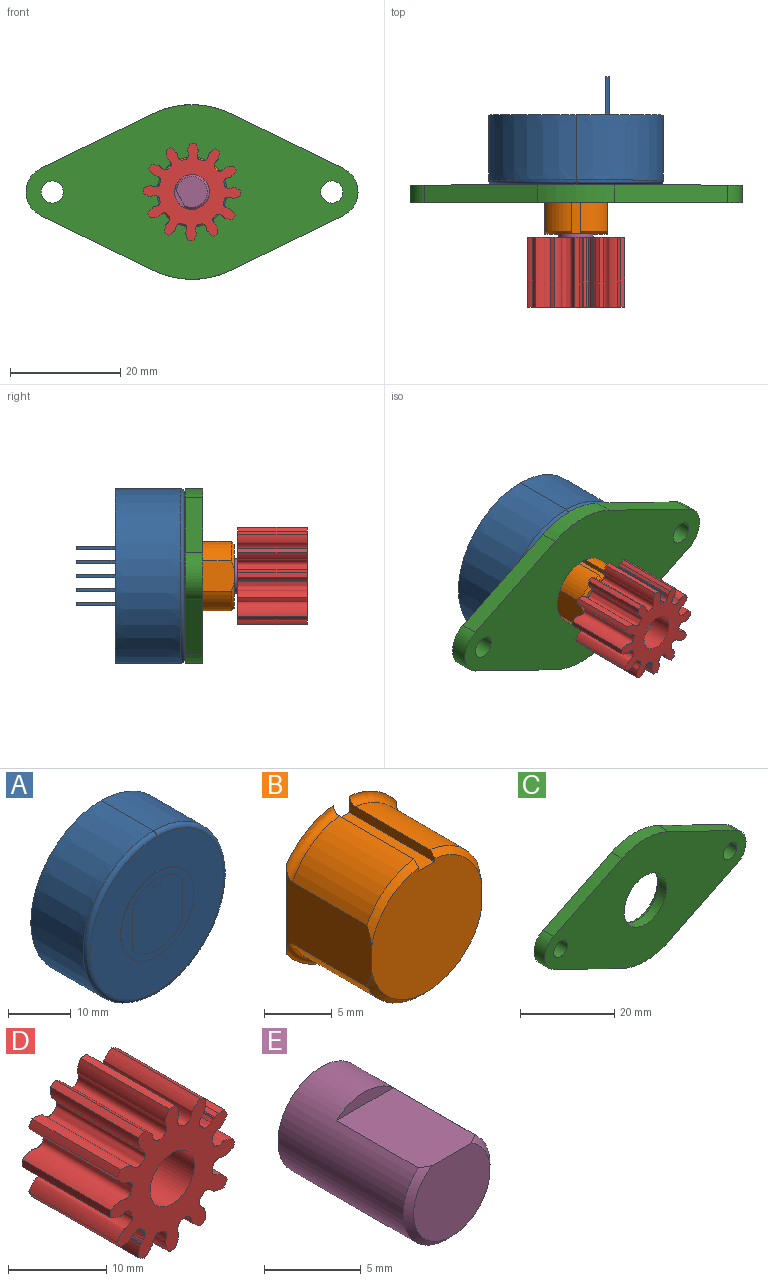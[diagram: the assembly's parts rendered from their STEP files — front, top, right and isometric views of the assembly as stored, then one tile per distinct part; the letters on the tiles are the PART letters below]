
ASSEMBLY  parts=5 mates=4
PART A: 35 faces, bbox 31.8x19.7x31.8 mm
  f0: plane 30.16x30.16mm, normal (0,-1,0), area 500mm2, adj f29,f30,f32,f33
  f1: plane 31.75x31.75mm, normal (0,1,0), area 789.7mm2, adj f2,f3,f5,f6,f7,f8,f10,f11
  f2: extruded ~31.75x15.88mm, area 589.6mm2, adj f1,f3,f32
  f3: extruded ~31.75x15.88mm, area 589.6mm2, adj f1,f2,f33
  f4: plane 0.64x0.64mm, normal (0,1,0), area 0.4mm2, adj f5,f6,f7,f8
  f5: plane 6.99x0.64mm, normal (0,0,-1), area 4.4mm2, adj f1,f4,f6,f8
  f6: plane 6.99x0.64mm, normal (1,0,0), area 4.4mm2, adj f1,f4,f5,f7
  f7: plane 6.99x0.64mm, normal (0,0,1), area 4.4mm2, adj f1,f4,f6,f8
  f8: plane 6.99x0.64mm, normal (-1,0,0), area 4.4mm2, adj f1,f4,f5,f7
  f9: plane 0.64x0.64mm, normal (0,1,0), area 0.4mm2, adj f10,f11,f12,f13
  f10: plane 6.99x0.64mm, normal (0,0,-1), area 4.4mm2, adj f1,f9,f11,f12
  f11: plane 6.99x0.64mm, normal (1,0,0), area 4.4mm2, adj f1,f9,f10,f13
  f12: plane 6.99x0.64mm, normal (-1,0,0), area 4.4mm2, adj f1,f9,f10,f13
  f13: plane 6.99x0.64mm, normal (0,0,1), area 4.4mm2, adj f1,f9,f11,f12
  f14: plane 0.64x0.64mm, normal (0,1,0), area 0.4mm2, adj f15,f16,f17,f18
  f15: plane 6.99x0.64mm, normal (-1,0,0), area 4.4mm2, adj f1,f14,f16,f17
  f16: plane 6.99x0.64mm, normal (0,0,1), area 4.4mm2, adj f1,f14,f15,f18
  f17: plane 6.99x0.64mm, normal (0,0,-1), area 4.4mm2, adj f1,f14,f15,f18
  f18: plane 6.99x0.64mm, normal (1,0,0), area 4.4mm2, adj f1,f14,f16,f17
  f19: plane 0.64x0.64mm, normal (0,1,0), area 0.4mm2, adj f20,f21,f22,f23
  f20: plane 6.99x0.64mm, normal (0,0,-1), area 4.4mm2, adj f1,f19,f21,f23
  f21: plane 6.99x0.64mm, normal (1,0,0), area 4.4mm2, adj f1,f19,f20,f22
  f22: plane 6.99x0.64mm, normal (0,0,1), area 4.4mm2, adj f1,f19,f21,f23
  f23: plane 6.99x0.64mm, normal (-1,0,0), area 4.4mm2, adj f1,f19,f20,f22
  f24: plane 0.64x0.64mm, normal (0,1,0), area 0.4mm2, adj f25,f26,f27,f28
  f25: plane 6.99x0.64mm, normal (0,0,-1), area 4.4mm2, adj f1,f24,f26,f28
  f26: plane 6.99x0.64mm, normal (1,0,0), area 4.4mm2, adj f1,f24,f25,f27
  f27: plane 6.99x0.64mm, normal (0,0,1), area 4.4mm2, adj f1,f24,f26,f28
  f28: plane 6.99x0.64mm, normal (-1,0,0), area 4.4mm2, adj f1,f24,f25,f27
  f29: extruded ~16.51x8.26mm, area 2.6mm2, adj f0,f30,f31
  f30: extruded ~16.51x8.26mm, area 2.6mm2, adj f0,f29,f31
  f31: plane 16.51x16.51mm, normal (0,-1,0), area 77.2mm2, adj f29,f30,f34
  f32: bspline ~31.75x25.88mm, area 61.3mm2, adj f0,f2,f33
  f33: bspline ~31.75x25.88mm, area 61.3mm2, adj f0,f3,f32
  f34: plane 13.92x11.43mm, normal (0,-1,0), area 136.9mm2, adj f31
PART B: 16 faces, bbox 14.5x8.9x16.1 mm
  f0: cone r=5.84mm half-angle=45deg, axis (0,1,0), area 10.7mm2, adj f3,f5,f13,f14
  f1: cone r=5.84mm half-angle=45deg, axis (0,1,0), area 4.7mm2, adj f3,f6,f12,f13
  f2: cone r=5.84mm half-angle=45deg, axis (0,1,0), area 4.7mm2, adj f3,f4,f10,f14
  f3: plane 11.62x11.43mm, normal (0,-1,0), area 106.2mm2, adj f0,f1,f2,f10,f11,f12,f13,f14
  f4: cylinder r=6.35mm len=7.75mm, axis (0,1,0), area 48.6mm2, adj f2,f9,f10,f14
  f5: cylinder r=6.35mm len=11.43mm, axis (0,1,0), area 110.2mm2, adj f0,f7,f13,f14
  f6: cylinder r=6.35mm len=7.75mm, axis (0,1,0), area 48.6mm2, adj f1,f8,f12,f13
  f7: torus R=6.99mm, axis (0,1,0), area 13.8mm2, adj f5,f13,f14,f15
  f8: torus R=6.99mm, axis (0,1,0), area 6.1mm2, adj f6,f12,f13,f15
  f9: torus R=6.99mm, axis (0,1,0), area 6.1mm2, adj f4,f10,f14,f15
  f10: plane 8.92x1.5mm, normal (-1,0,0), area 7.4mm2, adj f2,f3,f4,f9,f11,f15
  f11: plane 8.89x1.68mm, normal (0,0,1), area 14.9mm2, adj f3,f10,f12,f15
  f12: plane 8.92x1.5mm, normal (1,0,0), area 7.4mm2, adj f1,f3,f6,f8,f11,f15
  f13: plane 8.89x8.03mm, normal (-1,0,0), area 48.9mm2, adj f0,f1,f3,f5,f6,f7,f8,f15
  f14: plane 8.89x8.03mm, normal (1,0,0), area 48.9mm2, adj f0,f2,f3,f4,f5,f7,f9,f15
  f15: plane 13.92x11.43mm, normal (0,1,0), area 136.9mm2, adj f7,f8,f9,f10,f11,f12,f13,f14
PART C: 14 faces, bbox 60.3x3.2x31.8 mm
  f0: plane 20.54x9.99mm, normal (-0.44,0,-0.9), area 72.5mm2, adj f1,f7,f11,f12
  f1: cylinder r=15.88mm len=13.89mm, axis (0,1,0), area 45.6mm2, adj f0,f2,f11,f12
  f2: plane 20.54x9.99mm, normal (0.44,0,-0.9), area 72.5mm2, adj f1,f3,f11,f12
  f3: cylinder r=4.76mm len=8.57mm, axis (0,1,0), area 33.8mm2, adj f2,f4,f11,f12
  f4: plane 20.54x9.99mm, normal (0.44,0,0.9), area 72.5mm2, adj f3,f5,f11,f12
  f5: cylinder r=15.88mm len=13.89mm, axis (0,1,0), area 45.6mm2, adj f4,f6,f11,f12
  f6: plane 20.54x9.99mm, normal (-0.44,0,0.9), area 72.5mm2, adj f5,f7,f11,f12
  f7: cylinder r=4.76mm len=8.57mm, axis (0,1,0), area 33.8mm2, adj f0,f6,f11,f12
  f8: cylinder r=2.02mm len=4.04mm, axis (0,1,0), area 40.3mm2, adj f11,f12
  f9: cylinder r=2.02mm len=4.04mm, axis (0,1,0), area 40.3mm2, adj f11,f12
  f10: cylinder r=6.35mm len=12.7mm, axis (0,1,0), area 95mm2, adj f11,f13
  f11: plane 60.33x31.75mm, normal (0,-1,0), area 1069.4mm2, adj f0,f1,f2,f3,f4,f5,f6,f7
  f12: plane 60.33x31.75mm, normal (0,1,0), area 1035.7mm2, adj f0,f1,f2,f3,f4,f5,f6,f7
  f13: torus R=7.14mm, axis (0,-1,0), area 52mm2, adj f10,f12
PART D: 67 faces, bbox 18x19.2x18 mm
  f0: plane 17.95x17.95mm, normal (0,-1,0), area 141.6mm2, adj f1,f2,f3,f4,f5,f6,f7,f8
  f1: bspline ~19x1.59mm, area 19.4mm2, adj f0,f42,f53,f64
  f2: bspline ~19x0.24mm, area 1mm2, adj f0,f54,f55,f64
  f3: bspline ~19x0.35mm, area 2.9mm2, adj f0,f55,f56,f64
  f4: bspline ~19x0.28mm, area 0.9mm2, adj f0,f56,f57,f64
  f5: bspline ~19x0.24mm, area 0.6mm2, adj f0,f57,f58,f64
  f6: bspline ~19x0.2mm, area 0.4mm2, adj f0,f58,f59,f64
  f7: bspline ~19x0.5mm, area 3.2mm2, adj f0,f59,f60,f64
  f8: bspline ~19x0.49mm, area 5.4mm2, adj f0,f60,f61,f64
  f9: bspline ~19x0.28mm, area 1.3mm2, adj f0,f61,f62,f64
  f10: bspline ~19x0.95mm, area 10.1mm2, adj f0,f41,f62,f64
  f11: bspline ~19x1.59mm, area 19.4mm2, adj f0,f35,f44,f64
  f12: bspline ~19x0.24mm, area 1mm2, adj f0,f45,f46,f64
  f13: bspline ~19x0.35mm, area 2.9mm2, adj f0,f46,f47,f64
  f14: bspline ~19x0.28mm, area 0.9mm2, adj f0,f47,f48,f64
  f15: bspline ~19x0.24mm, area 0.6mm2, adj f0,f48,f49,f64
  f16: bspline ~19x0.2mm, area 0.4mm2, adj f0,f49,f50,f64
  f17: bspline ~19x0.5mm, area 3.2mm2, adj f0,f50,f51,f64
  f18: bspline ~19x0.49mm, area 5.4mm2, adj f0,f51,f52,f64
  f19: bspline ~19x0.28mm, area 1.3mm2, adj f0,f52,f63,f64
  f20: bspline ~19x0.95mm, area 10.1mm2, adj f0,f36,f63,f64
  f21: bspline ~19x3.59mm, area 91.1mm2, adj f0,f40,f42,f64
  f22: bspline ~19x3.59mm, area 91.1mm2, adj f0,f39,f40,f64
  f23: bspline ~19x3.56mm, area 91.1mm2, adj f0,f38,f39,f64
  f24: bspline ~19x3.59mm, area 91.1mm2, adj f0,f37,f38,f64
  f25: bspline ~19x3.59mm, area 91.1mm2, adj f0,f36,f37,f64
  f26: bspline ~19x3.59mm, area 91.1mm2, adj f0,f34,f35,f64
  f27: bspline ~19x3.59mm, area 91.1mm2, adj f0,f33,f34,f64
  f28: bspline ~19x3.56mm, area 91.1mm2, adj f0,f32,f33,f64
  f29: bspline ~19x3.59mm, area 91.1mm2, adj f0,f32,f43,f64
  f30: bspline ~19x3.59mm, area 91.1mm2, adj f0,f41,f43,f64
  f31: cylinder r=3.17mm len=12.7mm, axis (0,-1,0), area 252.9mm2, adj f0,f64
  f32: cylinder r=8.89mm len=12.7mm, axis (0,-1,0), area 11.5mm2, adj f0,f28,f29,f64
  f33: cylinder r=8.89mm len=12.7mm, axis (0,-1,0), area 11.5mm2, adj f0,f27,f28,f64
  f34: cylinder r=8.89mm len=12.7mm, axis (0,-1,0), area 11.5mm2, adj f0,f26,f27,f64
  f35: cylinder r=8.89mm len=12.7mm, axis (0,-1,0), area 11.5mm2, adj f0,f11,f26,f64
  f36: cylinder r=8.89mm len=12.7mm, axis (0,-1,0), area 11.5mm2, adj f0,f20,f25,f64
  f37: cylinder r=8.89mm len=12.7mm, axis (0,-1,0), area 11.5mm2, adj f0,f24,f25,f64
  f38: cylinder r=8.89mm len=12.7mm, axis (0,-1,0), area 11.5mm2, adj f0,f23,f24,f64
  f39: cylinder r=8.89mm len=12.7mm, axis (0,-1,0), area 11.5mm2, adj f0,f22,f23,f64
  f40: cylinder r=8.89mm len=12.7mm, axis (0,-1,0), area 11.5mm2, adj f0,f21,f22,f64
  f41: cylinder r=8.89mm len=12.7mm, axis (0,-1,0), area 11.5mm2, adj f0,f10,f30,f64
  f42: cylinder r=8.89mm len=12.7mm, axis (0,-1,0), area 11.5mm2, adj f0,f1,f21,f64
  f43: cylinder r=8.89mm len=12.7mm, axis (0,-1,0), area 11.5mm2, adj f0,f29,f30,f64
  f44: extruded ~12.7x0.04mm, area 0.6mm2, adj f0,f11,f64,f66
  f45: extruded ~12.7x0.05mm, area 0.8mm2, adj f0,f12,f64,f66
  f46: extruded ~12.7x0.11mm, area 1.9mm2, adj f0,f12,f13,f64
  f47: extruded ~12.7x0.61mm, area 8.6mm2, adj f0,f13,f14,f64
  f48: extruded ~12.7x0.15mm, area 2mm2, adj f0,f14,f15,f64
  f49: extruded ~12.7x0.16mm, area 2.3mm2, adj f0,f15,f16,f64
  f50: extruded ~12.7x0.45mm, area 8.1mm2, adj f0,f16,f17,f64
  f51: extruded ~12.7x0.89mm, area 12.3mm2, adj f0,f17,f18,f64
  f52: extruded ~12.7x0.09mm, area 1.5mm2, adj f0,f18,f19,f64
  f53: extruded ~12.7x0.04mm, area 0.6mm2, adj f0,f1,f64,f65
  f54: extruded ~12.7x0.05mm, area 0.8mm2, adj f0,f2,f64,f65
  f55: extruded ~12.7x0.11mm, area 1.9mm2, adj f0,f2,f3,f64
  f56: extruded ~12.7x0.61mm, area 8.6mm2, adj f0,f3,f4,f64
  f57: extruded ~12.7x0.15mm, area 2mm2, adj f0,f4,f5,f64
  f58: extruded ~12.7x0.16mm, area 2.3mm2, adj f0,f5,f6,f64
  f59: extruded ~12.7x0.45mm, area 8.1mm2, adj f0,f6,f7,f64
  f60: extruded ~12.7x0.89mm, area 12.3mm2, adj f0,f7,f8,f64
  f61: extruded ~12.7x0.09mm, area 1.5mm2, adj f0,f8,f9,f64
  f62: extruded ~12.7x0.61mm, area 8.1mm2, adj f0,f9,f10,f64
  f63: extruded ~12.7x0.61mm, area 8.1mm2, adj f0,f19,f20,f64
  f64: plane 17.95x17.95mm, normal (0,1,0), area 138.5mm2, adj f1,f2,f3,f4,f5,f6,f7,f8
  f65: bspline ~19x0.27mm, area 0.1mm2, adj f53,f54,f64
  f66: bspline ~19x0.27mm, area 0.1mm2, adj f44,f45,f64
PART E: 6 faces, bbox 6.3x9.5x6.3 mm
  f0: cylinder r=3.17mm len=9.14mm, axis (0,1,0), area 155mm2, adj f1,f3,f4,f5
  f1: plane 4.16x0.78mm, normal (0,-1,0), area 2.2mm2, adj f0,f3
  f2: plane 5.58x5.18mm, normal (0,-1,0), area 23.7mm2, adj f3,f5
  f3: plane 6.35x4.16mm, normal (0,0,1), area 26.2mm2, adj f0,f1,f2,f5
  f4: plane 6.34x6.34mm, normal (0,1,0), area 31.6mm2, adj f0
  f5: cone r=3.17mm half-angle=45deg, axis (0,1,0), area 8mm2, adj f0,f2,f3
PLACE A t=(-15.88,-6.17,15.88)mm
PLACE B t=(-15.88,-6.17,15.88)mm
PLACE C t=(-15.88,-6.17,15.88)mm
PLACE D rot(axis=(0,-1,0),28.7deg) t=(0,-9.55,0)mm
PLACE E rot(axis=(0,-1,0),118.7deg) t=(-6.29,-6.17,-21.55)mm
MATE fastened B.f0 <-> A.f34  axis (0,1,0) through (0,3.18,0)mm
MATE fastened C.f1 <-> A.f34  axis (0,-1,0) through (0,3.18,0)mm
MATE fastened D.f31 <-> E.f0  axis (0,-1,0) through (0,-6.35,0)mm
MATE revolute E.f0 <-> A.f31  axis (0,1,0) through (0,-5.71,0)mm
